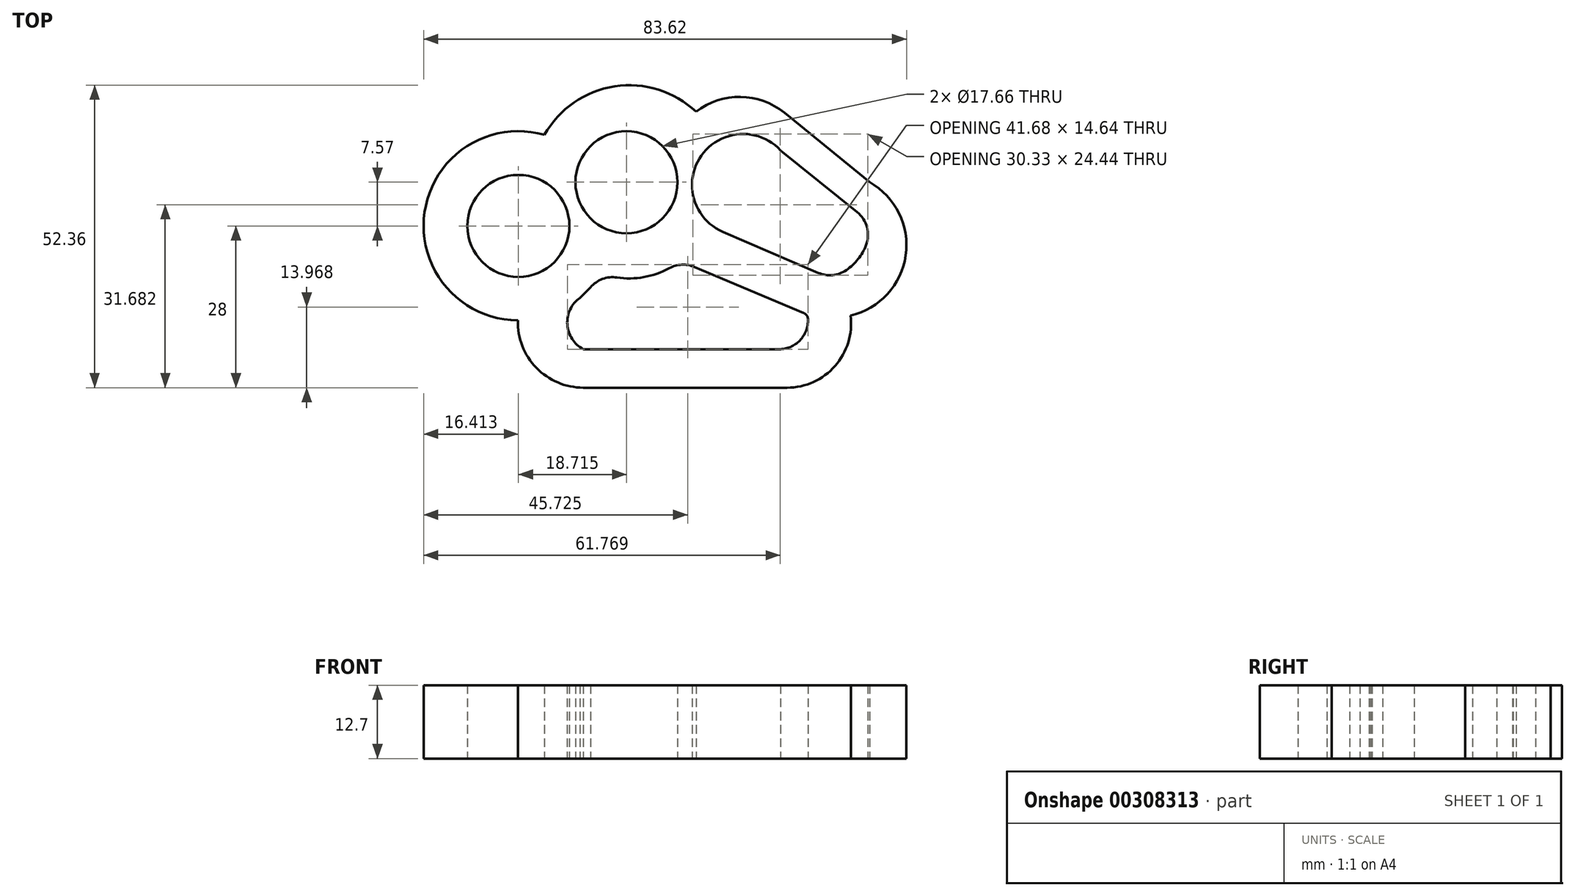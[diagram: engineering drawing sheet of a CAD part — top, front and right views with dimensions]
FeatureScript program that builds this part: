
annotation { "Feature Type Name" : "Feature", "Feature Type Description" : "" }
export const myFeature = defineFeature(function(context is Context, id is Id, definition is map)
    precondition{}
    {
        {
            var Q0;
            Q0=qCreatedBy(makeId("Top.planeOp"),FACE);
            var sketch = newSketch(context, id + "F0", { "sketchPlane" : qUnion([Q0])});
            skCircle(sketch, "E0", {"center": v(-10.85, 0) * mm, "radius": 8.83 * mm});
            skCircle(sketch, "E1", {"center": v(21.72, -3.49) * mm, "radius": 0.84 * mm});
            skCircle(sketch, "E2", {"center": v(-29.57, -7.57) * mm, "radius": 8.83 * mm});
            skLineSegment(sketch, "E3", {"start": v(15.83, 5.5) * mm, "end": v(29.08, -5.17) * mm});
            skLineSegment(sketch, "E4", {"start": v(22.37, -15.7) * mm, "end": v(5.84, -8.6) * mm});
            skArc(sketch, "E5", {"start": v(27.23, -15.21) * mm, "mid": v(29.25, -13.32) * mm, "end": v(30.62, -10.92) * mm});
            skArc(sketch, "E6", {"start": v(15.83, 5.5) * mm, "mid": v(2.12, 4.62) * mm, "end": v(5.84, -8.6) * mm});
            skPoint(sketch, "E7.visualSharp", {"position": v(31.22, -6.9) * mm});
            skArc(sketch, "E7.filletArc", {"start": v(30.95, -8.8) * mm, "mid": v(30.38, -6.74) * mm, "end": v(29, -5.1) * mm});
            skArc(sketch, "E8.filletArc", {"start": v(30.62, -10.92) * mm, "mid": v(30.79, -7.8) * mm, "end": v(29.08, -5.17) * mm});
            skPoint(sketch, "E9.visualSharp", {"position": v(24.35, -16.55) * mm});
            skArc(sketch, "E9.filletArc", {"start": v(22.37, -15.7) * mm, "mid": v(24.86, -16.08) * mm, "end": v(27.23, -15.21) * mm});
            skLineSegment(sketch, "E10", {"start": v(16.5, 12) * mm, "end": v(31.22, 0) * mm});
            skLineSegment(sketch, "E11", {"start": v(2.18, -15.21) * mm, "end": v(19.84, -22.66) * mm});
            skArc(sketch, "E12", {"start": v(1.2, 12.2) * mm, "mid": v(-12.9, 16.6) * mm, "end": v(-25.06, 8.2) * mm});
            skArc(sketch, "E13", {"start": v(16.5, 12) * mm, "mid": v(8.9, 14.77) * mm, "end": v(1.2, 12.2) * mm});
            skLineSegment(sketch, "E14", {"start": v(2.18, -15.21) * mm, "end": v(0.95, -14.69) * mm});
            skArc(sketch, "E15", {"start": v(-12.51, -16.5) * mm, "mid": v(-7.85, -16.43) * mm, "end": v(-3.45, -14.9) * mm});
            skPoint(sketch, "E16.visualSharp", {"position": v(-15.36, -15.77) * mm});
            skArc(sketch, "E16.filletArc", {"start": v(-12.51, -16.5) * mm, "mid": v(-15.02, -16.76) * mm, "end": v(-17.09, -18.2) * mm});
            skPoint(sketch, "E17.visualSharp", {"position": v(-1.51, -13.63) * mm});
            skArc(sketch, "E17.filletArc", {"start": v(0.95, -14.69) * mm, "mid": v(-1.27, -14.28) * mm, "end": v(-3.45, -14.9) * mm});
            skArc(sketch, "E18", {"start": v(-18.91, -20.02) * mm, "mid": v(-21.1, -24.64) * mm, "end": v(-18.31, -28.92) * mm});
            skArc(sketch, "E19", {"start": v(-25.06, 8.2) * mm, "mid": v(-45.8, -5.2) * mm, "end": v(-29.66, -23.9) * mm});
            skLineSegment(sketch, "E20", {"start": v(-17.09, -18.2) * mm, "end": v(-18.91, -20.02) * mm});
            skArc(sketch, "E21", {"start": v(27.94, -23.09) * mm, "mid": v(37.51, -12.67) * mm, "end": v(31.22, 0) * mm});
            skLineSegment(sketch, "E22", {"start": v(-18.31, -28.92) * mm, "end": v(15.56, -28.92) * mm});
            skArc(sketch, "E23", {"start": v(15.56, -28.92) * mm, "mid": v(19.17, -27.4) * mm, "end": v(20.59, -23.75) * mm});
            skLineSegment(sketch, "E24", {"start": v(-18.31, -35.57) * mm, "end": v(16.96, -35.57) * mm});
            skArc(sketch, "E25", {"start": v(16.96, -35.57) * mm, "mid": v(25.27, -31.8) * mm, "end": v(27.94, -23.09) * mm});
            skArc(sketch, "E26", {"start": v(-29.66, -23.9) * mm, "mid": v(-26.45, -32.13) * mm, "end": v(-18.31, -35.57) * mm});
            skPoint(sketch, "E27.visualSharp", {"position": v(20.5, -22.94) * mm});
            skArc(sketch, "E27.filletArc", {"start": v(20.59, -23.75) * mm, "mid": v(20.37, -23.1) * mm, "end": v(19.84, -22.66) * mm});
            skSolve(sketch);
        }
        {
            var Q0;
            Q0=qSketchRegion(id+"F0",true);
            extrude(context, id + "F1", {"entities" : qUnion([Q0]), "depth" : 12.7 * mm});
        }
    });
